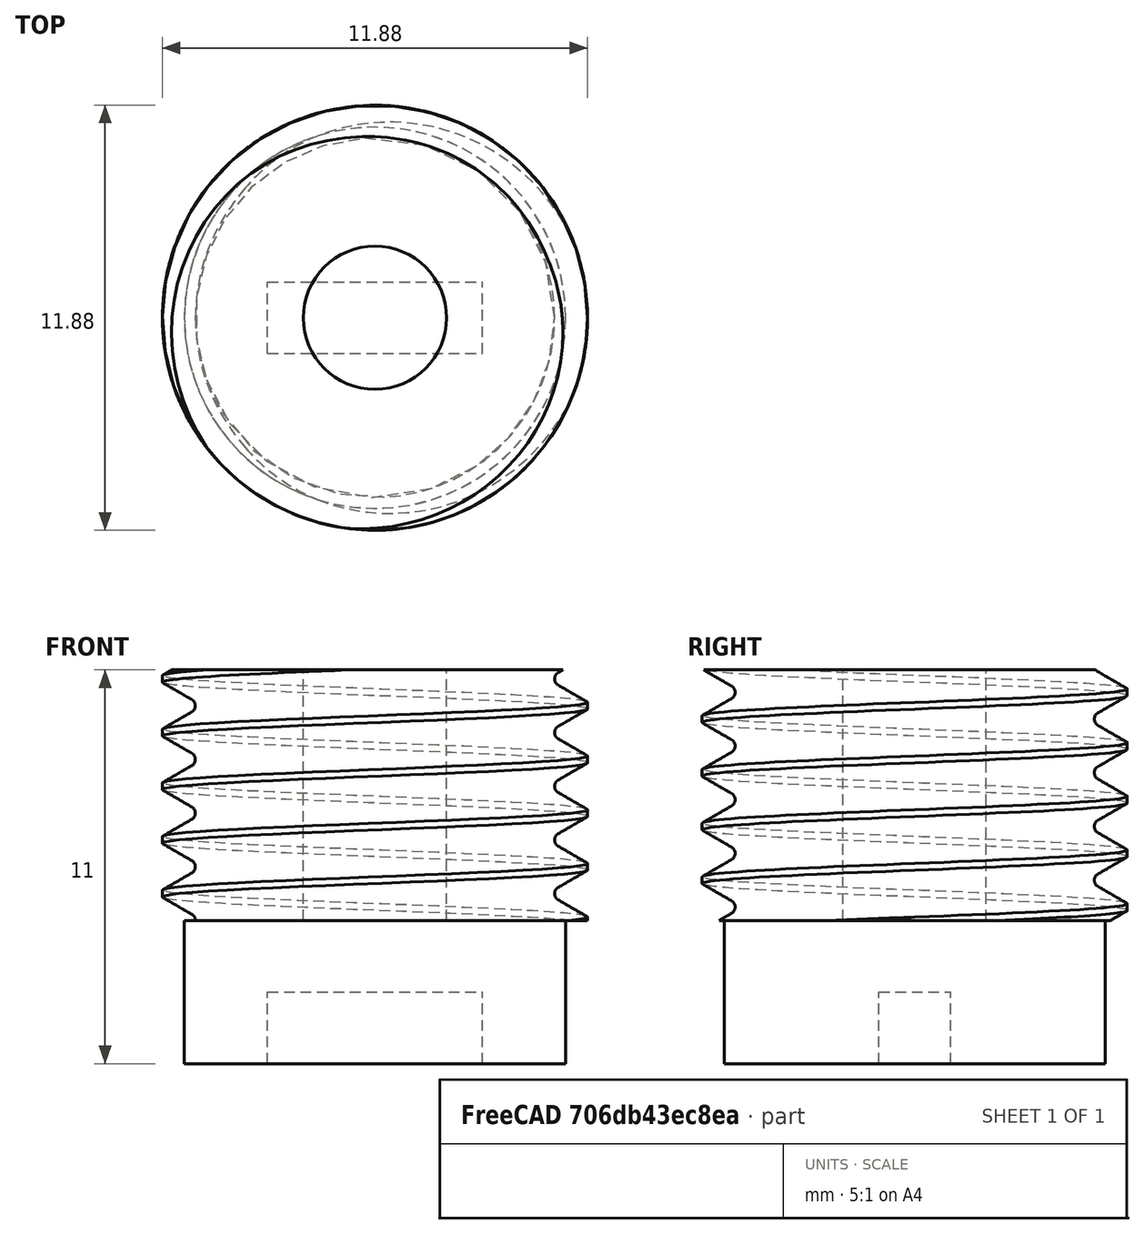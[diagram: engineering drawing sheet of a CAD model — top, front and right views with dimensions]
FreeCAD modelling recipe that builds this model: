
FCSTD DOCUMENT  (FreeCAD 0.17R13541 (Git))
Label: tip-changer-bolt
License: All rights reserved
LicenseURL: http://en.wikipedia.org/wiki/All_rights_reserved
objects: Part::Cylinder×3, Spreadsheet::Sheet×2, Part::Cut×2, Part::Helix×1, PartDesign::FeatureBase×1, Part::Box×1, Sketcher::SketchObject×1, PartDesign::SubtractivePipe×1, PartDesign::Body×1, Part::MultiFuse×1, Mesh::Feature×1
note: 13 computed .brp shape members not serialized (recipe doc carries the construction recipe); baked Part::Feature solids carry a one-line shape summary decoded from their .brp

FEATURE [Spreadsheet::Sheet] Spreadsheet
  cells = A1=steigung; B1=h; D1(pitch)=1.5; F1=bauhöhe; G1(height)=20; A2=Gewindetiefe; B2=t; C2=h*cos(30°); D2(threaddepth)==pitch * cos(30); F2=helix height; G2(height_h)=25; C3=threaddepth tol; D3(threaddepth_tol)==(pitch + tolerance * cos(30)) * cos(30); F3=Flanken - Tolerance; G3(tolerance)=0; A4=Nut; F4=Radien - Tolerance; G4(tolerance_rad)=0.20000000000000001; A5=ra; E5(nut_ra)==bolt_ri + bolt_si + threaddepth + nut_sa; A6=sa; E6(nut_sa)=3; A7=ri; E7(nut_ri)==nb_centerline - threaddepth / 2 + threaddepth / 4 + tolerance_rad; A9=Bolt; A10=ri; E10(bolt_ri)==E16; A11=si; E11(bolt_si)==E17; G11==sqrt(1 / 6 ^ 2 - (tan(30) / 4) ^ 2) * Spreadsheet.threaddepth_tol; A12=ra; E12(bolt_ra)==nb_centerline + threaddepth / 2 - threaddepth / 8 - tolerance_rad; A14=Nut/Bold centerline; E14(nb_centerline)==bolt_ri + bolt_si + threaddepth / 2; A16=Spring rh; E16(spring_rh)==Tabelle1.B18 / 2 + Tabelle1.B3; A17=hülsenstärke sh; E17(spring_sh)==Tabelle1.B19; A18=join rest   js; E18(spring_sj)=1.3999999999999999; A21=join heigtht jh; B21(spring_jh)=3; A22=join ri; B22(spring_jri)==spring_rh + spring_sh + tolerance
FEATURE [Part::Cylinder] Cylinder006  label="Zylinder006"
  Angle = 360
  AttacherType = Attacher::AttachEngine3D
  Height = 10
  Radius = 2.00001
  expr: Height = Tabelle1.B23
  expr: Radius = Spreadsheet.bolt_ri + 1.0000000000000001e-005
FEATURE [Part::Cylinder] Cylinder007  label="Zylinder007"
  Angle = 360
  AttacherType = Attacher::AttachEngine3D
  Height = 7
  Radius = 5.93666
  expr: Height = Tabelle1.B23 - Tabelle1.B19
  expr: Radius = Spreadsheet.bolt_ra
FEATURE [Part::Cut] Cut003
  Base = -> Cylinder007
  Tool = -> Cylinder006
FEATURE [Part::Helix] Helix003
  Angle = 0
  AttacherType = Attacher::AttachEngine3D
  Height = 25
  LocalCoord = 0
  Pitch = 1.5
  Radius = 5.93666
  Style = 1
  expr: Radius = Spreadsheet.bolt_ra
  expr: Height = Spreadsheet.height_h
  expr: Pitch = Spreadsheet.pitch
FEATURE [PartDesign::FeatureBase] BaseFeature003
  BaseFeature = -> Cut003
FEATURE [Part::Cylinder] Cylinder015  label="Zylinder015"
  Angle = 360
  AttacherType = Attacher::AttachEngine3D
  Height = 4
  Placement = pos=(0,0,0.75) rot=(0,0,1;0rad)
  Radius = 5.32476
  expr: Placement.Base.z = Spreadsheet.D1 / 2
  expr: Height = 4
  expr: Radius = Spreadsheet.E7 - Tabelle1.B3
FEATURE [Part::Box] Box  label="Quader"
  AttacherType = Attacher::AttachEngine3D
  Height = 2
  Length = 6
  Placement = pos=(-3,-1,0.75) rot=(0,0,1;0rad)
  Width = 2
  expr: Placement.Base.z = Spreadsheet.D1 / 2
FEATURE [Part::Cut] Cut007
  Base = -> Cylinder015
  Tool = -> Box
FEATURE [Spreadsheet::Sheet] Tabelle1
  cells = A1=Abstand Pip/Boden; B1=65; A3=Toleranz; B3=0.20000000000000001; A5=Teller; A6=Breite/Länge; B6=65; A7=Dicke; B7=5; A8=Befestigung höhe; B8=10; A10=Achse; A11=Durchmesser; B11=5; A12=Teller Befestigung; B12==B7 + B8; A13=Führung Länge; B13=40; C13=Wandstärke; D13=5; A14=Freiraum; B14=5; A15=Länge; B15==B14 + B13 + B12; A17=Feder; A18=Hülse durchmesser; B18=3.6000000000000001; A19=Hülse Wanddicke; B19=3; A20=L0; B20=25; A21=delta L; B21=3; A22=Spannmutter; A23=Höhe; B23=10; A24=Durchmesser Pitch; B24=20; A25=min Abstand Boden; B25=5; A28=min Oberkante Platte; B28==B25 + B23 + B20 + B19 + B13 + B7; A30=Gehäuse; A31=Wandstärke; B31=5; A32=Durchmesser; B32==B24 + 2 * B31; A33=Höhe; B33==B25 + B20 + B19 + B13; A35=Spitze d1; B35=7; A36=Spitze d2; B36=6.5; A37=Raster; B37=10.5; A38=Anzahl x/y; B38=6; A39=offset; B39==(Tabelle1.B6 - ((Tabelle1.B38 - 1) * Tabelle1.B37 + Tabelle1.B35)) / 2 + Tabelle1.B35 / 2
FEATURE [Sketcher::SketchObject] CopySketch003
  Placement = pos=(0,0,0) rot=(1,0,0;1.5708rad)
  expr: Constraints[26] = Spreadsheet.threaddepth_tol * (1 - 1 / 4 - 1 / 8) - sqrt(1 / 6 ^ 2 - (tan(30) / 4) ^ 2) * Spreadsheet.threaddepth_tol
  expr: Constraints[7] = Spreadsheet.threaddepth_tol * (1 - 1 / 8) * tan(30)
  expr: Constraints[1] = Spreadsheet.bolt_ra + 0.001
  expr: Constraints[17] = Spreadsheet.pitch / 2
  expr: Constraints[20] = Spreadsheet.threaddepth_tol * (1 - 1 / 4 - 1 / 8)
  sketch-geometry (9):
    g0: LineSegment [constr] StartX=0 StartY=0 StartZ=0 EndX=5.93766 EndY=0 EndZ=0
    g1: LineSegment StartX=5.93766 StartY=-0.09375 StartZ=0 EndX=5.93766 EndY=-0.75 EndZ=0
    g2: LineSegment StartX=5.93766 StartY=-0.75 StartZ=0 EndX=5.93766 EndY=-1.40625 EndZ=0
    g3: LineSegment StartX=5.93766 StartY=-0.09375 StartZ=0 EndX=5.12576 EndY=-0.5625 EndZ=0
    g4: LineSegment StartX=5.93766 StartY=-1.40625 StartZ=0 EndX=5.12576 EndY=-0.9375 EndZ=0
    g5: LineSegment [constr] StartX=5.12576 StartY=-0.5625 StartZ=0 EndX=5.12576 EndY=-0.9375 EndZ=0
    g6: LineSegment [constr] StartX=5.93766 StartY=-0.75 StartZ=0 EndX=5.93766 EndY=0 EndZ=0
    g7: LineSegment [constr] StartX=5.93766 StartY=-0.75 StartZ=0 EndX=5.23401 EndY=-0.75 EndZ=0
    g8: ArcOfCircle CenterX=5.23401 CenterY=-0.75 CenterZ=0 NormalX=0 NormalY=0 NormalZ=1 AngleXU=0 Radius=0.216506 StartAngle=2.0944 EndAngle=4.18879
  constraints (27):
    c: Horizontal(g0)
    c: DistanceX(g0,g0) = 5.93766
    c: Coincident(g-1,g0)
    c: Vertical(g1)
    c: Coincident(g2,g1)
    c: Vertical(g2)
    c: Equal(g1,g2)
    c: DistanceY(g1,g1) = 0.65625
    c: Coincident(g3,g1)
    c: Angle(g3,g1) = 1.0472
    c: Coincident(g4,g2)
    c: Angle(g2,g4) = 1.0472
    c: Vertical(g5)
    c: Coincident(g4,g5)
    c: Equal(g4,g3)
    c: Coincident(g6,g1)
    c: Vertical(g6)
    c: DistanceY(g6,g6) = 0.75
    c: Coincident(g6,g0)
    c: Coincident(g3,g5)
    c: DistanceX(g4,g4) = 0.811899
    c: Coincident(g7,g1)
    c: Horizontal(g7)
    c: Coincident(g8,g7)
    c: Coincident(g8,g3)
    c: Coincident(g8,g4)
    c: DistanceX(g7,g7) = 0.703646
FEATURE [PartDesign::SubtractivePipe] SubtractivePipe003
  AuxilleryCurvelinear = true
  AuxillerySpineTangent = false
  BaseFeature = -> BaseFeature003
  Binormal = (0,0,0)
  Mode = 2
  Profile = -> CopySketch003
  Spine = -> Helix003 [Edge1,Edge2,Edge3,Edge4,Edge5,Edge6,Edge7,Edge8,Edge9,Edge10,Edge11]
  SpineTangent = false
  Transformation = 0
  Transition = 0
FEATURE [PartDesign::Body] Body006  label="JoinBolt"
  BaseFeature = -> Cut003
  Group = -> [BaseFeature003,CopySketch003,SubtractivePipe003]
  Origin = -> Origin009
  Placement = pos=(0,0,4.75) rot=(0,0,1;0rad)
  Tip = -> SubtractivePipe003
  expr: Placement.Base.z = Spreadsheet.D1 / 2 + 4
FEATURE [Part::MultiFuse] Fusion006  label="tip-changer-bolt"
  Shapes = -> [Cut007,Body006]
FEATURE [Mesh::Feature] Mesh  label="tip-changer-bolt (Meshed)"
